# Revit family: KNS_KK_Поворот парапетный изм верт_IEK
name_source: partatom
category: Соединительные детали воздуховодов
units: mm (PartAtom-declared; Revit-internal decimal feet)

## family parameters
Всегда вертикально = Нет
На основе рабочей плоскости = Нет
Общий = Нет
При загрузке вырезать с полостями = Нет
Размер круглого соединителя = Использовать диаметр
Тип детали = Отвод

## types (1)
- Внешний
    ADSK_URL документации изделия = https://www.iek.ru
    ADSK_Версия Revit = 2019
    ADSK_Версия семейства = 1.1
    ADSK_Группирование = Кабельные короба
    ADSK_Единица измерения = шт
    ADSK_Завод-изготовитель = IEK
    ADSK_Марка = ПРАЙМЕР
    ADSK_Материал наименование = ПВХ (PVC)
    ADSK_Материал обозначение = Пластик
    ADSK_Обозначение = ТУ 27.33.14-004-83135016-2017
    IEK_Гарантийный срок = 2 года
    IEK_Монтажная температура = -15...+60 °C
    IEK_Описание = Поворот 90° КМП служит для соединения двух кабель-каналов одинакового типоразмера под углом 90°.
    IEK_Срок службы = 25 лет
    KSI_CMa_Строительные материалы = 01.07.14
    KSI_CPr_Строительные изделия = 20.2.05.06
    URL = https://www.iek.ru
    Длина вылета = 9 мм
    Изготовитель = IEK
    Стоимость = 0 $
    Угол поворота = 90.00°
